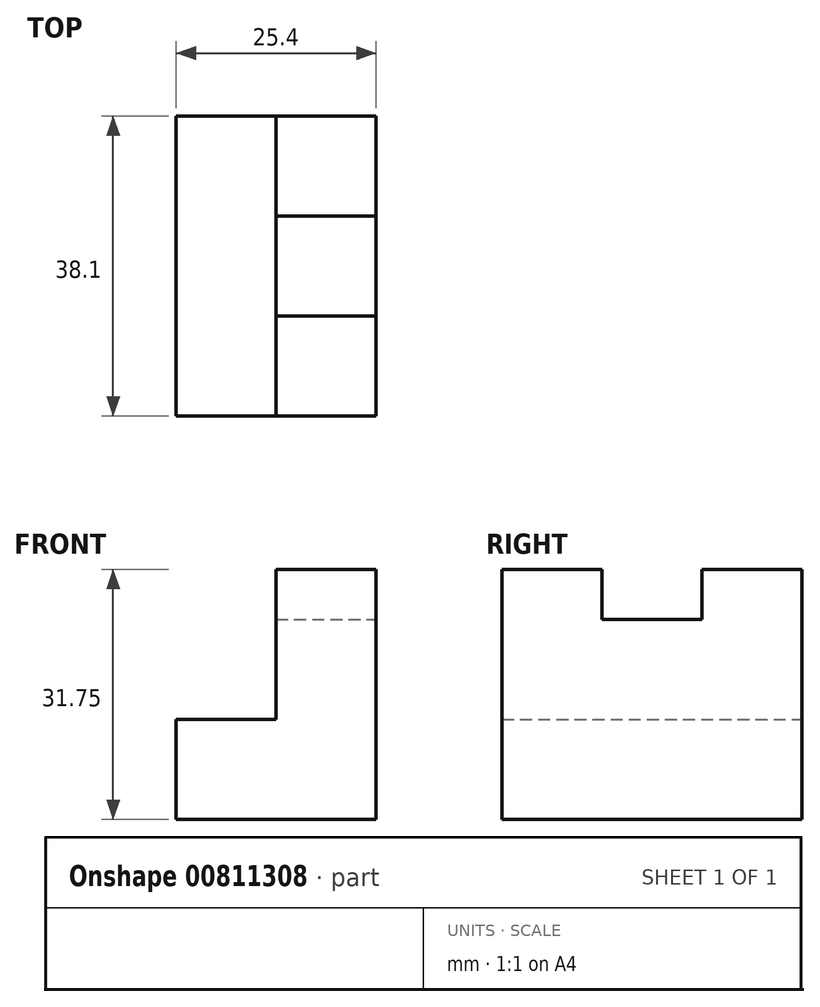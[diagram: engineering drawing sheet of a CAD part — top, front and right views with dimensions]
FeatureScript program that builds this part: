
annotation { "Feature Type Name" : "Feature", "Feature Type Description" : "" }
export const myFeature = defineFeature(function(context is Context, id is Id, definition is map)
    precondition{}
    {
        {
            var Q0;
            Q0=qCreatedBy(makeId("Front.planeOp"),FACE);
            var sketch = newSketch(context, id + "F0", { "sketchPlane" : qUnion([Q0])});
            skLineSegment(sketch, "E0", {"start": v(0, 0) * mm, "end": v(25.4, 0) * mm});
            skLineSegment(sketch, "E1", {"start": v(25.4, 0) * mm, "end": v(25.4, 31.75) * mm});
            skLineSegment(sketch, "E2", {"start": v(25.4, 31.75) * mm, "end": v(12.7, 31.75) * mm});
            skLineSegment(sketch, "E3", {"start": v(12.7, 31.75) * mm, "end": v(12.7, 12.7) * mm});
            skLineSegment(sketch, "E4", {"start": v(12.7, 12.7) * mm, "end": v(0, 12.7) * mm});
            skLineSegment(sketch, "E5", {"start": v(0, 12.7) * mm, "end": v(0, 0) * mm});
            skSolve(sketch);
        }
        {
            var Q0;
            Q0 = qSketchRegion(id + "F0", true);
            extrude(context, id + "F1", {"entities" : qUnion([Q0]), "depth" : 12.7 * mm, "offsetDistance" : 25.4 * mm});
        }
        {
            var Q0;
            Q0=makeQuery(id+"F1.opExtrude","CAP_FACE",FACE,{"disambiguationData":[OSD([sQuery(id+"F0.wireOp",EDGE,"E0"),sQuery(id+"F0.wireOp",EDGE,"E1"),sQuery(id+"F0.wireOp",EDGE,"E2"),sQuery(id+"F0.wireOp",EDGE,"E3"),sQuery(id+"F0.wireOp",EDGE,"E4"),sQuery(id+"F0.wireOp",EDGE,"E5")])],"isStart":false});
            var sketch = newSketch(context, id + "F2", { "sketchPlane" : qUnion([Q0])});
            skLineSegment(sketch, "E6", {"start": v(12.7, 12.7) * mm, "end": v(12.7, 25.4) * mm});
            skLineSegment(sketch, "E7", {"start": v(12.7, 25.4) * mm, "end": v(25.4, 25.4) * mm});
            skLineSegment(sketch, "E8", {"start": v(25.4, 25.4) * mm, "end": v(25.4, 0) * mm});
            skLineSegment(sketch, "E9", {"start": v(25.4, 0) * mm, "end": v(0, 0) * mm});
            skLineSegment(sketch, "E10", {"start": v(0, 0) * mm, "end": v(0, 12.7) * mm});
            skLineSegment(sketch, "E11", {"start": v(0, 12.7) * mm, "end": v(12.7, 12.7) * mm});
            skSolve(sketch);
        }
        {
            var Q0;
            Q0 = qSketchRegion(id + "F2", true);
            extrude(context, id + "F3", {"entities" : qUnion([Q0]), "operationType" : NewBodyOperationType.ADD, "depth" : 12.7 * mm, "offsetDistance" : 25.4 * mm});
        }
        {
            var Q0;
            Q0=makeQuery(id+"F3.opExtrude","CAP_FACE",FACE,{"disambiguationData":[OSD([sQuery(id+"F2.wireOp",EDGE,"E6"),sQuery(id+"F2.wireOp",EDGE,"E7"),sQuery(id+"F2.wireOp",EDGE,"E8"),sQuery(id+"F2.wireOp",EDGE,"E9"),sQuery(id+"F2.wireOp",EDGE,"E10"),sQuery(id+"F2.wireOp",EDGE,"E11")])],"isStart":false});
            var sketch = newSketch(context, id + "F4", { "sketchPlane" : qUnion([Q0])});
            skLineSegment(sketch, "E12", {"start": v(12.7, 12.7) * mm, "end": v(12.7, 31.75) * mm});
            skLineSegment(sketch, "E13", {"start": v(12.7, 31.75) * mm, "end": v(25.4, 31.75) * mm});
            skLineSegment(sketch, "E14", {"start": v(25.4, 31.75) * mm, "end": v(25.4, 0) * mm});
            skLineSegment(sketch, "E15", {"start": v(25.4, 0) * mm, "end": v(0, 0) * mm});
            skLineSegment(sketch, "E16", {"start": v(0, 0) * mm, "end": v(0, 12.7) * mm});
            skLineSegment(sketch, "E17", {"start": v(0, 12.7) * mm, "end": v(12.7, 12.7) * mm});
            skSolve(sketch);
        }
        {
            var Q0;
            Q0 = qSketchRegion(id + "F4", true);
            extrude(context, id + "F5", {"entities" : qUnion([Q0]), "operationType" : NewBodyOperationType.ADD, "depth" : 12.7 * mm, "offsetDistance" : 25.4 * mm});
        }
    });
